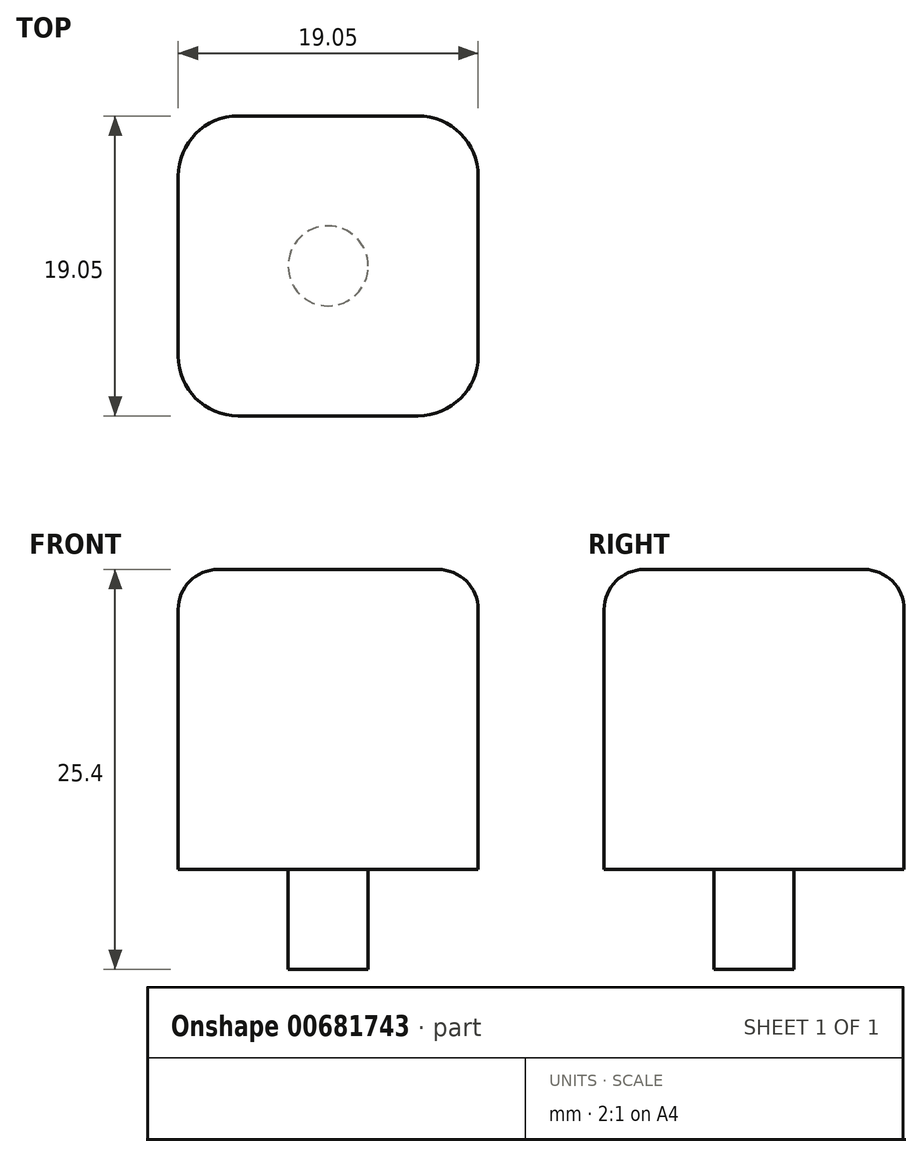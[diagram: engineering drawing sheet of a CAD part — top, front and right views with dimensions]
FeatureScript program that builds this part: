
annotation { "Feature Type Name" : "Feature", "Feature Type Description" : "" }
export const myFeature = defineFeature(function(context is Context, id is Id, definition is map)
    precondition{}
    {
        {
            var Q0;
            Q0=qCreatedBy(makeId("Top.planeOp"),FACE);
            var sketch = newSketch(context, id + "F0", { "sketchPlane" : qUnion([Q0])});
            skLineSegment(sketch, "E0.bottom", {"start": v(-49.57, 25.58) * mm, "end": v(-30.52, 25.58) * mm});
            skLineSegment(sketch, "E0.top", {"start": v(-49.57, 44.63) * mm, "end": v(-30.52, 44.63) * mm});
            skLineSegment(sketch, "E0.left", {"start": v(-49.57, 25.58) * mm, "end": v(-49.57, 44.63) * mm});
            skLineSegment(sketch, "E0.right", {"start": v(-30.52, 25.58) * mm, "end": v(-30.52, 44.63) * mm});
            skSolve(sketch);
        }
        {
            var Q0;
            Q0=makeQuery(id+"F0.imprint","IMPRINT",FACE,{"disambiguationData":[TD([[makeQuery(id+"F0.imprint","IMPRINT",EDGE,{"derivedFrom":sQuery(id+"F0.wireOp",EDGE,"E0.bottom")}),1.0]])]});
            extrude(context, id + "F1", {"entities" : qUnion([Q0]), "depth" : 19.05 * mm, "offsetDistance" : 25.4 * mm});
        }
        {
            var Q0;
            Q0=makeQuery(id+"F1.opExtrude","CAP_FACE",FACE,{"disambiguationData":[OSD([sQuery(id+"F0.wireOp",EDGE,"E0.bottom"),sQuery(id+"F0.wireOp",EDGE,"E0.top"),sQuery(id+"F0.wireOp",EDGE,"E0.left"),sQuery(id+"F0.wireOp",EDGE,"E0.right")])],"isStart":false});
            fillet(context, id + "F2", {"entities" : qUnion([Q0]), "radius" : 2.54 * mm, "tangentPropagation" : true, "allowEdgeOverflow" : false});
        }
        {
            var Q0;
            Q0=makeQuery(id+"F1.opExtrude","SWEPT_EDGE",EDGE,{"disambiguationData":[OSD([sQuery(id+"F0.wireOp",EDGE,"E0.bottom"),sQuery(id+"F0.wireOp",EDGE,"E0.left")])]});
            var Q1;
            Q1=makeQuery(id+"F1.opExtrude","SWEPT_EDGE",EDGE,{"disambiguationData":[OSD([sQuery(id+"F0.wireOp",EDGE,"E0.top"),sQuery(id+"F0.wireOp",EDGE,"E0.left")])]});
            var Q2;
            Q2=makeQuery(id+"F1.opExtrude","SWEPT_EDGE",EDGE,{"disambiguationData":[OSD([sQuery(id+"F0.wireOp",EDGE,"E0.bottom"),sQuery(id+"F0.wireOp",EDGE,"E0.right")])]});
            var Q3;
            Q3=makeQuery(id+"F1.opExtrude","SWEPT_EDGE",EDGE,{"disambiguationData":[OSD([sQuery(id+"F0.wireOp",EDGE,"E0.top"),sQuery(id+"F0.wireOp",EDGE,"E0.right")])]});
            fillet(context, id + "F3", {"entities" : qUnion([Q0, Q1, Q2, Q3]), "radius" : 3.8 * mm, "tangentPropagation" : true, "allowEdgeOverflow" : false});
        }
        {
            var Q0;
            Q0=makeQuery(id+"F1.opExtrude","CAP_FACE",FACE,{"disambiguationData":[OSD([sQuery(id+"F0.wireOp",EDGE,"E0.bottom"),sQuery(id+"F0.wireOp",EDGE,"E0.top"),sQuery(id+"F0.wireOp",EDGE,"E0.left"),sQuery(id+"F0.wireOp",EDGE,"E0.right")])],"isStart":true});
            var sketch = newSketch(context, id + "F4", { "sketchPlane" : qUnion([Q0])});
            skCircle(sketch, "E1", {"center": v(-40.05, -35.1) * mm, "radius": 2.54 * mm});
            skSolve(sketch);
        }
        {
            var Q0;
            Q0=makeQuery(id+"F4.imprint","IMPRINT",FACE,{"disambiguationData":[TD([[makeQuery(id+"F4.imprint","IMPRINT",EDGE,{"derivedFrom":sQuery(id+"F4.wireOp",EDGE,"E1")}),1.0]])]});
            extrude(context, id + "F5", {"entities" : qUnion([Q0]), "operationType" : NewBodyOperationType.ADD, "depth" : 6.35 * mm, "offsetDistance" : 25.4 * mm});
        }
    });
